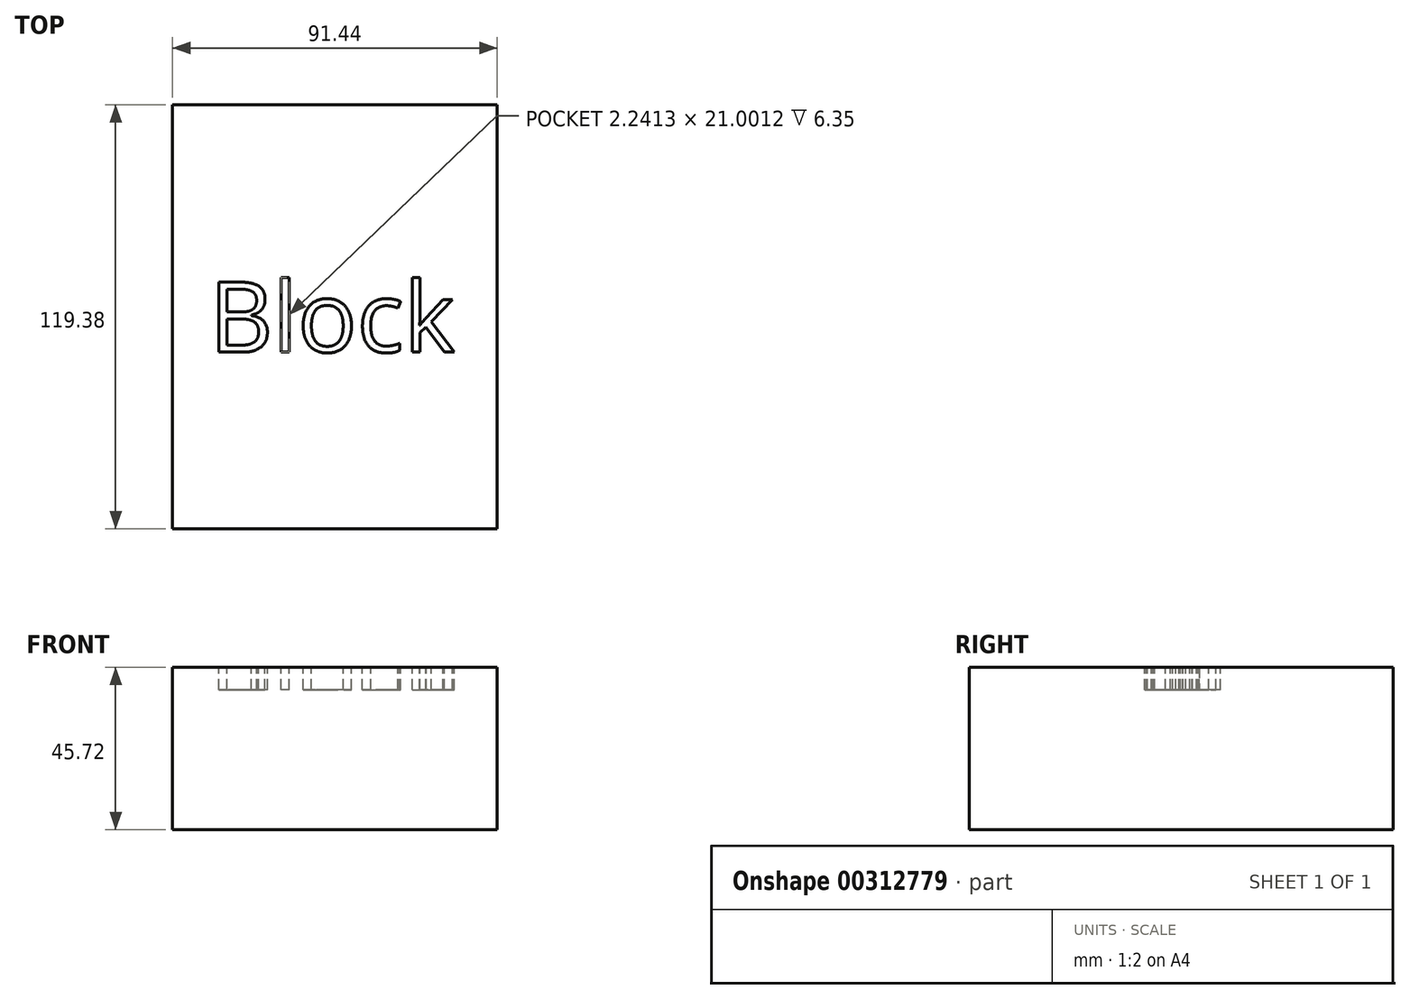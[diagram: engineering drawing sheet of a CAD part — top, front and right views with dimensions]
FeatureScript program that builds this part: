
annotation { "Feature Type Name" : "Feature", "Feature Type Description" : "" }
export const myFeature = defineFeature(function(context is Context, id is Id, definition is map)
    precondition{}
    {
        {
            var Q0;
            Q0=qCreatedBy(makeId("Top.planeOp"),FACE);
            var sketch = newSketch(context, id + "F0", { "sketchPlane" : qUnion([Q0])});
            skLineSegment(sketch, "E0.bottom", {"start": v(0, 0) * mm, "end": v(91.44, 0) * mm});
            skLineSegment(sketch, "E0.top", {"start": v(0, 119.38) * mm, "end": v(91.44, 119.38) * mm});
            skLineSegment(sketch, "E0.left", {"start": v(0, 0) * mm, "end": v(0, 119.38) * mm});
            skLineSegment(sketch, "E0.right", {"start": v(91.44, 0) * mm, "end": v(91.44, 119.38) * mm});
            skSolve(sketch);
        }
        {
            var Q0;
            Q0 = qSketchRegion(id + "F0", true);
            extrude(context, id + "F1", {"entities" : qUnion([Q0]), "depth" : 45.72 * mm});
        }
        {
            var Q0;
            Q0=makeQuery(id+"F1.opExtrude","CAP_FACE",FACE,{"disambiguationData":[OSD([sQuery(id+"F0.wireOp",EDGE,"E0.bottom"),sQuery(id+"F0.wireOp",EDGE,"E0.top"),sQuery(id+"F0.wireOp",EDGE,"E0.left"),sQuery(id+"F0.wireOp",EDGE,"E0.right")])],"isStart":false});
            var sketch = newSketch(context, id + "F2", { "sketchPlane" : qUnion([Q0])});
            skText(sketch, "E1", { "text": "Block", "fontName": "OpenSans-Regular.ttf"});
            skLineSegment(sketch, "E2", {"start": v(10.33, 59.7) * mm, "end": v(0, 59.7) * mm, "construction": true});
            skLineSegment(sketch, "E3", {"start": v(45.72, 69.64) * mm, "end": v(45.72, 119.38) * mm});
            const initialGuessF2  = {"E1": [0.01033, 0.04974, 1, 0, 0.0199]};
            skSetInitialGuess(sketch, initialGuessF2);
            skSolve(sketch);
        }
        {
            var Q0;
            Q0 = qSketchRegion(id + "F2", true);
            extrude(context, id + "F3", {"entities" : qUnion([Q0]), "operationType" : NewBodyOperationType.REMOVE, "oppositeDirection" : true, "depth" : 6.35 * mm});
        }
    });
